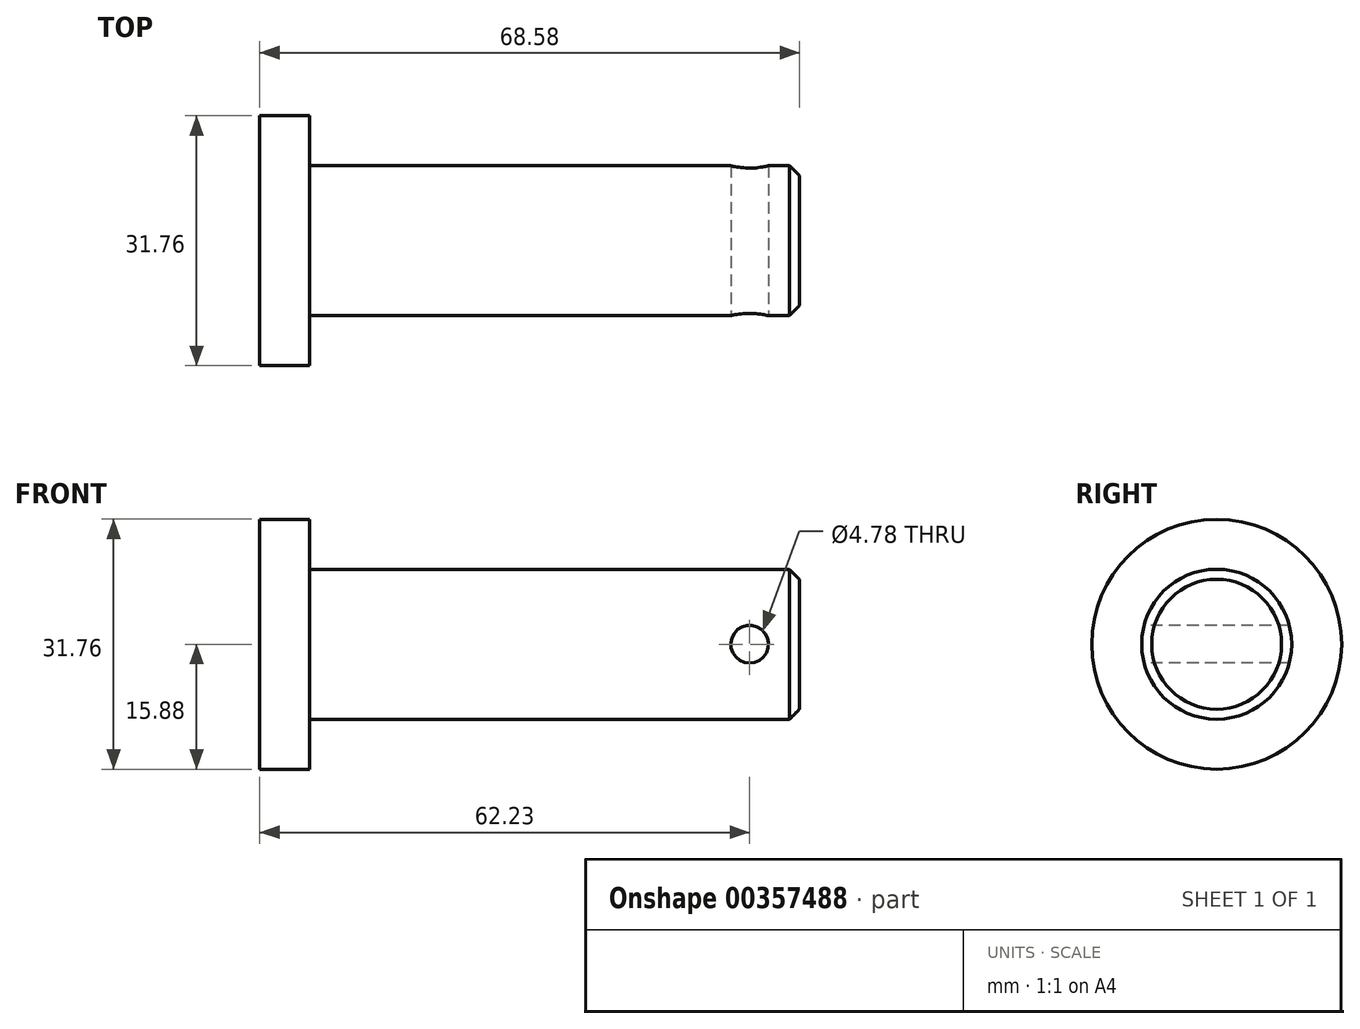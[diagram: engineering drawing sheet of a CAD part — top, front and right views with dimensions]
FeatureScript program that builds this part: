
annotation { "Feature Type Name" : "Feature", "Feature Type Description" : "" }
export const myFeature = defineFeature(function(context is Context, id is Id, definition is map)
    precondition{}
    {
        {
            var Q0;
            Q0=qCreatedBy(makeId("Right.planeOp"),FACE);
            var sketch = newSketch(context, id + "F0", { "sketchPlane" : qUnion([Q0])});
            skCircle(sketch, "E0", {"center": v(0, 0) * mm, "radius": 15.88 * mm});
            skSolve(sketch);
        }
        {
            var Q0;
            Q0 = qSketchRegion(id + "F0", true);
            extrude(context, id + "F1", {"entities" : qUnion([Q0]), "depth" : 6.35 * mm});
        }
        {
            var Q0;
            Q0=makeQuery(id+"F1.opExtrude","CAP_FACE",FACE,{"disambiguationData":[OSD([sQuery(id+"F0.wireOp",EDGE,"E0")])],"isStart":false});
            var sketch = newSketch(context, id + "F2", { "sketchPlane" : qUnion([Q0])});
            skCircle(sketch, "E1", {"center": v(0, 0) * mm, "radius": 9.53 * mm});
            skSolve(sketch);
        }
        {
            var Q0;
            Q0 = qSketchRegion(id + "F2", true);
            extrude(context, id + "F3", {"entities" : qUnion([Q0]), "operationType" : NewBodyOperationType.ADD, "depth" : 62.23 * mm});
        }
        {
            var Q0;
            Q0=makeQuery(id+"F3.opExtrude","CAP_EDGE",EDGE,{"disambiguationData":[OSD([sQuery(id+"F2.wireOp",EDGE,"E1")])],"isStart":false});
            chamfer(context, id + "F4", {"entities" : qUnion([Q0]), "chamferType" : ChamferType.OFFSET_ANGLE, "width" : 1.27 * mm, "oppositeDirection" : false, "angle" : 45 * degree, "tangentPropagation" : true});
        }
        {
            var Q0;
            Q0=qCreatedBy(makeId("Front.planeOp"),FACE);
            var sketch = newSketch(context, id + "F5", { "sketchPlane" : qUnion([Q0])});
            skCircle(sketch, "E2", {"center": v(62.23, 0) * mm, "radius": 2.39 * mm});
            skSolve(sketch);
        }
        {
            var Q0;
            Q0 = qSketchRegion(id + "F5", true);
            extrude(context, id + "F6", {"entities" : qUnion([Q0]), "operationType" : NewBodyOperationType.REMOVE, "endBound" : BoundingType.THROUGH_ALL, "oppositeDirection" : true, "depth" : 25.4 * mm, "hasSecondDirection" : true, "secondDirectionOppositeDirection" : false, "secondDirectionDepth" : 25.4 * mm});
        }
    });
